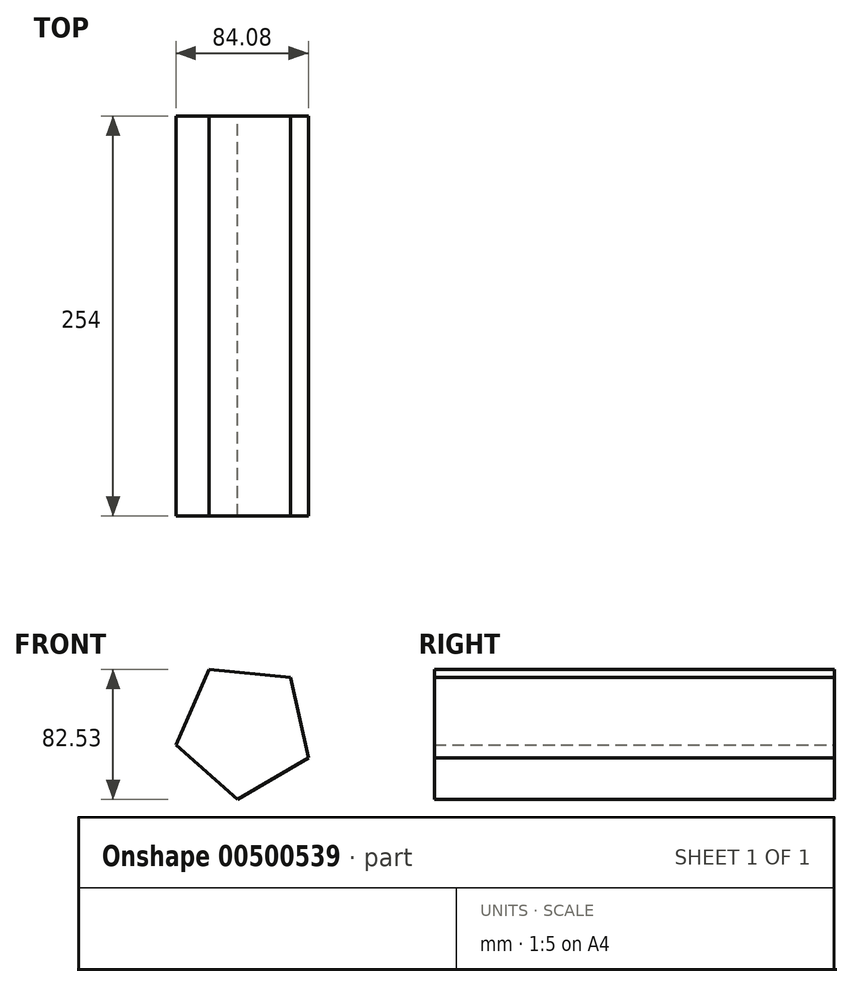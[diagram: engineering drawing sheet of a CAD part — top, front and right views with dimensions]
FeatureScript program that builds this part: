
annotation { "Feature Type Name" : "Feature", "Feature Type Description" : "" }
export const myFeature = defineFeature(function(context is Context, id is Id, definition is map)
    precondition{}
    {
        {
            var Q0;
            Q0=qCreatedBy(makeId("Front.planeOp"),FACE);
            var sketch = newSketch(context, id + "F0", { "sketchPlane" : qUnion([Q0])});
            skCircle(sketch, "E0.cCircle", {"center": v(0, 0) * mm, "radius": 44.42 * mm, "construction": true});
            skLineSegment(sketch, "E0.0", {"start": v(-22.44, 38.33) * mm, "end": v(29.52, 33.19) * mm});
            skLineSegment(sketch, "E0.1", {"start": v(29.52, 33.19) * mm, "end": v(40.69, -17.82) * mm});
            skLineSegment(sketch, "E0.2", {"start": v(40.69, -17.82) * mm, "end": v(-4.37, -44.2) * mm});
            skLineSegment(sketch, "E0.3", {"start": v(-4.37, -44.2) * mm, "end": v(-43.39, -9.5) * mm});
            skLineSegment(sketch, "E0.4", {"start": v(-43.39, -9.5) * mm, "end": v(-22.44, 38.33) * mm});
            skSolve(sketch);
        }
        {
            var Q0;
            Q0=makeQuery(id+"F0.imprint","IMPRINT",FACE,{"disambiguationData":[TD([[makeQuery(id+"F0.imprint","IMPRINT",EDGE,{"derivedFrom":sQuery(id+"F0.wireOp",EDGE,"E0.0")}),-1.0]])]});
            extrude(context, id + "F1", {"entities" : qUnion([Q0]), "depth" : 254 * mm});
        }
    });
